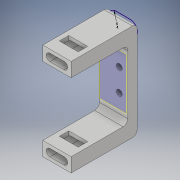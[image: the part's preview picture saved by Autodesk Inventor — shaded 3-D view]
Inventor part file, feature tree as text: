
AUTODESK INVENTOR PART (.ipt)
format: ipt  version: 2019 (Build 230136000, 136)  size: 420,864 bytes
history: native  units: mm
features: sketch x5, extrude x4, other x3, plane x2, mirror x1, fillet x1
ambient origin geometry x8: Origin, YZ Plane, XZ Plane, XY Plane, X Axis, Y Axis, Z Axis, Center Point
bodies: Solid1 (feature_tree)
feature tree (16):
  sketch  "Sketch1"  dims[d0=12.0mm d1=29.0mm]
  plane  "Work Plane1"
  plane  "Work Plane2"
  extrude  "Extrusion1"  Depth=12.0mm
  sketch  "Sketch8"  dims[d2=4.95mm d3=2.5mm]
  extrude  "Extrusion8"  Depth=2.5mm
  extrude  "Extrusion9"  Depth=2.5mm
  sketch  "Sketch10"  dims[d6=2.5mm d7=4.69mm d8=2.5mm]
  extrude  "Extrusion10"  Depth=4.69mm
  mirror  "Mirror3"
  fillet  "Fillet6"  Radius=2.5mm
  sketch  "Sketch9"  dims[d4=4.81mm d5=2.5mm]
  sketch  "Sketch11"  dims[d9=4.0mm d10=0.0mm d60=17.5mm d61=3.0mm d62=3.1mm d63=6.0mm d64=12.0mm d65=4.0mm d66=24.0mm d67=0.0mm d68=0.0mm d69=200.0mm d70=0.0mm d71=6.0mm d72=5.0mm d73=4.0mm d74=4.0mm d75=4.0mm d76=4.0mm d77=200.0mm d78=0.0mm d79=2.0mm]
  other  "<userpath>\Desktop\PWR\SEM7\INZYNIER\maszyna\Maszyna1.iam"
  other  "Maszyna1.iam"
  other  "endstop_maszyna:1"
